# Revit family: TY-B-TY4851_Metric
name_source: partatom
category: Sprinklers
units: mm (PartAtom-declared; Revit-internal decimal feet)

## family parameters
Always vertical = Yes
Cut with Voids When Loaded = No
Maintain Annotation Orientation = No
OmniClass Number = 23.65.70.17.11.24
OmniClass Title = Fire Fighting Sprinkler Heads
Part Type = Normal
Room Calculation Point = No
Round Connector Dimension = Use Diameter
Shared = No
Work Plane-Based = No

## types (42) — shared parameters
COBie = Yes
COBie.Component.Name = Sprinklers:Upright_SIN
COBie.Type = Yes
COBie.Type.AssetType = Fixed
COBie.Type.Category = Pr_70_55_97_84:Sprinklers
COBie.Type.DurationUnit = year
COBie.Type.Manufacturer = Tyco Fire Protection Products
COBie.Type.Material = Bronze
COBie.Type.Shape = Cylinder
COBie.Type.Size = 1/2"(DN15)
Coverage = Standard
Coverage_ = Standard
K-Factor = 114.87
Manufacturer = Tyco Fire Protection Products
Manufacturer URL = www.tyco-fire.com
Material_ = Bronze
Model = TY-B
Nominal Diameter 1 = 15 mm
Orifice = Extra Large
Orifice Size = 13 mm
Outside Diameter 1 = 21 mm
Response = Standard
Response_ = Standard
SIN No = TY4851
Takeout 1 = 56 mm
Technical Data Sheet No = TFP151
zero-valued in all types: COBie.Type.NominalHeight, COBie.Type.NominalLength, COBie.Type.NominalWidth, COBie.Type.ReplacementCost, Default Elevation, Style Id

## per-type parameters (varying)
| type | COBie.Component.Description | COBie.Type.Colour | COBie.Type.Finish | COBie.Type.ModelNumber | COBie.Type.ModelReference | COBie.Type.WarrantyGuarantorParts | Description | Finish_ | Part No | Temperature Rating |
| Upright ½" NPT 57°C  Brass_57-560-1-135 | TY-B Wet Upright  135°F K8.0 1/2 NPT Br | Yellow | Natural Brass | 57-560-1-135 | TY-B Wet Upright  135°F K8.0 1/2 NPT Br | http://tycofsbp.com
TFPPTerms_of_Sale.pdf | TY-B Upright Brass 57°C 8K ½" NPT | Natural Brass | 57-560-1-135 | 57 °C |
| Upright ½" NPT 68°C Brass_57-560-1-155 | TY-B Wet Upright  155°F K8.0 1/2 NPT Br | Yellow | Natural Brass | 57-560-1-155 | TY-B Wet Upright  155°F K8.0 1/2 NPT Br | http://tycofsbp.com
TFPPTerms_of_Sale.pdf | TY-B Upright Brass 68°C 8K ½" NPT | Natural Brass | 57-560-1-155 | 68 °C |
| Upright ½" NPT 79°C Brass_57-560-1-175 | TY-B Wet Upright  175°F K8.0 1/2 NPT Br | Yellow | Natural Brass | 57-560-1-175 | TY-B Wet Upright  175°F K8.0 1/2 NPT Br | http://tycofsbp.com
TFPPTerms_of_Sale.pdf | TY-B Upright Brass 79°C 8K ½" NPT | Natural Brass | 57-560-1-175 | 79 °C |
| Upright ½" NPT 93°C Brass_57-560-1-200 | TY-B Wet Upright  200°F K8.0 1/2 NPT Br | Yellow | Natural Brass | 57-560-1-200 | TY-B Wet Upright  200°F K8.0 1/2 NPT Br | http://tycofsbp.com
TFPPTerms_of_Sale.pdf | TY-B Upright Brass 93°C 8K ½" NPT | Natural Brass | 57-560-1-200 | 93 °C |
| Upright ½" NPT 141°C Brass_57-560-1-286 | TY-B Wet Upright  286°F K8.0 1/2 NPT Br | Yellow | Natural Brass | 57-560-1-286 | TY-B Wet Upright  286°F K8.0 1/2 NPT Br | http://tycofsbp.com
TFPPTerms_of_Sale.pdf | TY-B Upright Brass 141°C 8K ½" NPT | Natural Brass | 57-560-1-286 | 141 °C |
| Upright ½" NPT 182°C Brass_57-560-1-360 | TY-B Wet Upright  360°F K8.0 1/2 NPT Br | Yellow | Natural Brass | 57-560-1-360 | TY-B Wet Upright  360°F K8.0 1/2 NPT Br | http://tycofsbp.com
TFPPTerms_of_Sale.pdf | TY-B Upright Brass 182°C 8K ½" NPT | Natural Brass | 57-560-1-360 | 182 °C |
| Upright ½" NPT 57°C White_57-560-3-135 | TY-B Wet Upright  135°F K8.0 1/2 NPT Wh9010 | White | Pure White | 57-560-3-135 | TY-B Wet Upright  135°F K8.0 1/2 NPT Wh9010 | http://tycofsbp.com
TFPPTerms_of_Sale.pdf | TY-B Upright White 57°C 8K ½" NPT | White RAL9010 | 57-560-3-135 | 57 °C |
| Upright ½" NPT 68°C White_57-560-3-155 | TY-B Wet Upright  155°F K8.0 1/2 NPT Wh9010 | White | Pure White | 57-560-3-155 | TY-B Wet Upright  155°F K8.0 1/2 NPT Wh9010 | http://tycofsbp.com
TFPPTerms_of_Sale.pdf | TY-B Upright White 68°C 8K ½" NPT | White RAL9010 | 57-560-3-155 | 68 °C |
| Upright ½" NPT 79°C White_57-560-3-175 | TY-B Wet Upright  175°F K8.0 1/2 NPT Wh9010 | White | Pure White | 57-560-3-175 | TY-B Wet Upright  175°F K8.0 1/2 NPT Wh9010 | http://tycofsbp.com
TFPPTerms_of_Sale.pdf | TY-B Upright White 79°C 8K ½" NPT | White RAL9010 | 57-560-3-175 | 79 °C |
| Upright ½" NPT 93°C White_57-560-3-200 | TY-B Wet Upright  200°F K8.0 1/2 NPT Wh9010 | White | Pure White | 57-560-3-200 | TY-B Wet Upright  200°F K8.0 1/2 NPT Wh9010 | http://tycofsbp.com
TFPPTerms_of_Sale.pdf | TY-B Upright White 93°C 8K ½" NPT | White RAL9010 | 57-560-3-200 | 93 °C |
| Upright ½" NPT 141°C White_57-560-3-286 | TY-B Wet Upright  286°F K8.0 1/2 NPT Wh9010 | White | Pure White | 57-560-3-286 | TY-B Wet Upright  286°F K8.0 1/2 NPT Wh9010 | http://tycofsbp.com
TFPPTerms_of_Sale.pdf | TY-B Upright White 141°C 8K ½" NPT | White RAL9010 | 57-560-3-286 | 141 °C |
| Upright ½" NPT 182°C White_57-560-3-360 | TY-B Wet Upright  360°F K8.0 1/2 NPT Wh9010 | White | Pure White | 57-560-3-360 | TY-B Wet Upright  360°F K8.0 1/2 NPT Wh9010 | http://tycofsbp.com
TFPPTerms_of_Sale.pdf | TY-B Upright White 182°C 8K ½" NPT | White RAL9010 | 57-560-3-360 | 182 °C |
| Upright ½" NPT 57°C White_57-560-4-135 | TY-B Wet Upright  135°F K8.0 1/2 NPT Wh9003 | White | Signal White | 57-560-4-135 | TY-B Wet Upright  135°F K8.0 1/2 NPT Wh9003 | http://tycofsbp.com | TY-B Upright White 57°C 8K ½" NPT | White RAL9003 | 57-560-4-135 | 57 °C |
| Upright ½" NPT 68°C White_57-560-4-155 | TY-B Wet Upright  155°F K8.0 1/2 NPT Wh9003 | White | Signal White | 57-560-4-155 | TY-B Wet Upright  155°F K8.0 1/2 NPT Wh9003 | http://tycofsbp.com | TY-B Upright White 68°C 8K ½" NPT | White RAL9003 | 57-560-4-155 | 68 °C |
| Upright ½" NPT 79°C White_57-560-4-175 | TY-B Wet Upright  175°F K8.0 1/2 NPT Wh9003 | White | Signal White | 57-560-4-175 | TY-B Wet Upright  175°F K8.0 1/2 NPT Wh9003 | http://tycofsbp.com | TY-B Upright White 79°C 8K ½" NPT | White RAL9003 | 57-560-4-175 | 79 °C |
| Upright ½" NPT 93°C White_57-560-4-200 | TY-B Wet Upright  200°F K8.0 1/2 NPT Wh9003 | White | Signal White | 57-560-4-200 | TY-B Wet Upright  200°F K8.0 1/2 NPT Wh9003 | http://tycofsbp.com | TY-B Upright White 93°C 8K ½" NPT | White RAL9003 | 57-560-4-200 | 93 °C |
| Upright ½" NPT 141°C White_57-560-4-286 | TY-B Wet Upright  286°F K8.0 1/2 NPT Wh9003 | White | Signal White | 57-560-4-286 | TY-B Wet Upright  286°F K8.0 1/2 NPT Wh9003 | http://tycofsbp.com | TY-B Upright White 141°C 8K ½" NPT | White RAL9003 | 57-560-4-286 | 141 °C |
| Upright ½" NPT 182°C White_57-560-4-360 | TY-B Wet Upright  360°F K8.0 1/2 NPT Wh9003 | White | Signal White | 57-560-4-360 | TY-B Wet Upright  360°F K8.0 1/2 NPT Wh9003 | http://tycofsbp.com | TY-B Upright White 182°C 8K ½" NPT | White RAL9003 | 57-560-4-360 | 182 °C |
| Upright ½" NPT 68°C JetBlack_57-560-5-155 | TY-B Wet Upright  155°F K8.0 1/2 NPT JBlk | Black | Jet Black | 57-560-5-155 | TY-B Wet Upright  155°F K8.0 1/2 NPT JBlk | http://tycofsbp.com | TY-B Upright JetBlack 68°C 8K ½" NPT | JetBlack RAL9005 | 57-560-5-155 | 68 °C |
| Upright ½" NPT 68°C  JetBlack_57-560-5-200 | TY-B Wet Upright_Black_155   155°F K8.0 1/2 NPT JBlk | Black | Jet Black | 57-560-5-200 | TY-B Wet Upright_Black_155   155°F K8.0 1/2 NPT JBlk | http://tycofsbp.com | TY-B Upright JetBlack 68°C 8K ½" NPT | Jet Black RAL9005 | 57-560-5-200 | 68 °C |
| Upright ½" NPT 57°C Wax_57-560-6-135 | TY-B Wet Upright  57.2°C K115 DN15 NPT Wx | Gray | Wax Coated | 57-560-6-135 | TY-B Wet Upright  57.2°C K115 DN15 NPT Wx | http://tycofsbp.com | TY-B Upright Wax 57°C 8K ½" NPT | Wax Coated | 57-560-6-135 | 57 °C |
| Upright ½" NPT 68°C Wax_57-560-6-155 | TY-B Wet Upright  68.3°C K115 DN15 NPT Wx | Gray | Wax Coated | 57-560-6-155 | TY-B Wet Upright  68.3°C K115 DN15 NPT Wx | http://tycofsbp.com | TY-B Upright Wax 68°C 8K ½" NPT | Wax Coated | 57-560-6-155 | 68 °C |
| Upright ½" NPT 79°C Wax_57-560-6-175 | TY-B Wet Upright  79.4°C K115 DN15 NPT Wx | Gray | Wax Coated | 57-560-6-175 | TY-B Wet Upright  79.4°C K115 DN15 NPT Wx | http://tycofsbp.com | TY-B Upright Wax 79°C 8K ½" NPT | Wax Coated | 57-560-6-175 | 79 °C |
| Upright ½" NPT 93°C Wax_57-560-6-200 | TY-B Wet Upright  93.3°C K115 DN15 NPT Wx | Gray | Wax Coated | 57-560-6-200 | TY-B Wet Upright  93.3°C K115 DN15 NPT Wx | http://tycofsbp.com | TY-B Upright Wax 93°C 8K ½" NPT | Wax Coated | 57-560-6-200 | 93 °C |
| Upright ½" NPT 141°C Wax_57-560-6-286 | TY-B Wet Upright  141.1°C K115 DN15 NPT Wx | Gray | Wax Coated | 57-560-6-286 | TY-B Wet Upright  141.1°C K115 DN15 NPT Wx | http://tycofsbp.com | TY-B Upright Wax 141°C 8K ½" NPT | Wax Coated | 57-560-6-286 | 141 °C |
| Upright ½" NPT 57°C  Lead_57-560-7-135 | TY-B Wet Upright  57.2°C K115 DN15 NPT Lead | Gray | Lead Coated | 57-560-7-135 | TY-B Wet Upright  57.2°C K115 DN15 NPT Lead | http://tycofsbp.com | TY-B Upright Lead 57°C 8K ½" NPT | Lead Coated | 57-560-7-135 | 57 °C |
| Upright ½" NPT 68°C Lead_57-560-7-155 | TY-B Wet Upright  68.3°C K115 DN15 NPT Lead | Gray | Lead Coated | 57-560-7-155 | TY-B Wet Upright  68.3°C K115 DN15 NPT Lead | http://tycofsbp.com | TY-B Upright Lead 68°C 8K ½" NPT | Lead Coated | 57-560-7-155 | 68 °C |
| Upright ½" NPT 79°C Lead_57-560-7-175 | TY-B Wet Upright  79.4°C K115 DN15 NPT Lead | Gray | Lead Coated | 57-560-7-175 | TY-B Wet Upright  79.4°C K115 DN15 NPT Lead | http://tycofsbp.com | TY-B Upright Lead 79°C 8K ½" NPT | Lead Coated | 57-560-7-175 | 79 °C |
| Upright ½" NPT 93°C Lead_57-560-7-200 | TY-B Wet Upright  93.3°C K115 DN15 NPT Lead | Gray | Lead Coated | 57-560-7-200 | TY-B Wet Upright  93.3°C K115 DN15 NPT Lead | http://tycofsbp.com | TY-B Upright Lead 93°C 8K ½" NPT | Lead Coated | 57-560-7-200 | 93 °C |
| Upright ½" NPT 141°C Lead_57-560-7-286 | TY-B Wet Upright  141.1°C K115 DN15 NPT Lead | Gray | Lead Coated | 57-560-7-286 | TY-B Wet Upright  141.1°C K115 DN15 NPT Lead | http://tycofsbp.com | TY-B Upright Lead 141°C 8K ½" NPT | Lead Coated | 57-560-7-286 | 141 °C |
| Upright ½" NPT 182°C Lead_57-560-7-360 | TY-B Wet Upright  182.2°C K115 DN15 NPT Lead | Gray | Lead Coated | 57-560-7-360 | TY-B Wet Upright  182.2°C K115 DN15 NPT Lead | http://tycofsbp.com | TY-B Upright Lead 182°C 8K ½" NPT | Lead Coated | 57-560-7-360 | 182 °C |
| Upright ½" NPT 57°C Wax Over Lead_57-560-8-135 | TY-B Wet Upright  57.2°C K115 DN15 NPT WoL | Gray | Wax Over Lead | 57-560-8-135 | TY-B Wet Upright  57.2°C K115 DN15 NPT WoL | http://tycofsbp.com | TY-B Upright Wax over Lead 57°C 8K ½" NPT | Wax Over Lead | 57-560-8-135 | 57 °C |
| Upright ½" NPT 68°C Wax Over Lead_57-560-8-155 | TY-B Wet Upright  68.3°C K115 DN15 NPT WoL | Gray | Wax Over Lead | 57-560-8-155 | TY-B Wet Upright  68.3°C K115 DN15 NPT WoL | http://tycofsbp.com | TY-B Upright Wax over Lead 68°C 8K ½" NPT | Wax Over Lead | 57-560-8-155 | 68 °C |
| Upright ½" NPT 79°C Wax Over Lead_57-560-8-175 | TY-B Wet Upright  79.4°C K115 DN15 NPT WoL | Gray | Wax Over Lead | 57-560-8-175 | TY-B Wet Upright  79.4°C K115 DN15 NPT WoL | http://tycofsbp.com | TY-B Upright Wax over Lead 79°C 8K ½" NPT | Wax Over Lead | 57-560-8-175 | 79 °C |
| Upright ½" NPT 93°C Wax Over Lead_57-560-8-200 | TY-B Wet Upright  93.3°C K115 DN15 NPT WoL | Gray | Wax Over Lead | 57-560-8-200 | TY-B Wet Upright  93.3°C K115 DN15 NPT WoL | http://tycofsbp.com | TY-B Upright Wax over Lead 93°C 8K ½" NPT | Wax Over Lead | 57-560-8-200 | 93 °C |
| Upright ½" NPT 141°C Wax Over Lead_57-560-8-286 | TY-B Wet Upright  141.1°C K115 DN15 NPT WoL | Gray | Wax over Lead | 57-560-8-286 | TY-B Wet Upright  141.1°C K115 DN15 NPT WoL | http://tycofsbp.com | TY-B Upright Wax over Lead 141°C 8K ½" NPT | Wax Over Lead | 57-560-8-286 | 141 °C |
| Upright ½" NPT 57°C Chrome_57-560-9-135 | TY-B Wet Upright  135°F K8.0 1/2 NPT Chr | White | Pure White | 57-560-9-135 | TY-B Wet Upright  135°F K8.0 1/2 NPT Chr | http://tycofsbp.com
TFPPTerms_of_Sale.pdf | TY-B Upright Chrome 57°C 8K ½" NPT | Chrome Plated | 57-560-9-135 | 57 °C |
| Upright ½" NPT 68°C Chrome_57-560-9-155 | TY-B Wet Upright  155°F K8.0 1/2 NPT Chr | Silver | Chrome Plated | 57-560-9-155 | TY-B Wet Upright  155°F K8.0 1/2 NPT Chr | http://tycofsbp.com
TFPPTerms_of_Sale.pdf | TY-B Upright Chrome 68°C 8K ½" NPT | Chrome Plated | 57-560-9-155 | 68 °C |
| Upright ½" NPT 79°C Chrome_57-560-9-175 | TY-B Wet Upright  175°F K8.0 1/2 NPT Chr | Silver | Chrome Plated | 57-560-9-175 | TY-B Wet Upright  175°F K8.0 1/2 NPT Chr | http://tycofsbp.com
TFPPTerms_of_Sale.pdf | TY-B Upright Chrome 79°C 8K ½" NPT | Chrome Plated | 57-560-9-175 | 79 °C |
| Upright ½" NPT 93°C Chrome_57-560-9-200 | TY-B Wet Upright  200°F K8.0 1/2 NPT Chr | Silver | Chrome Plated | 57-560-9-200 | TY-B Wet Upright  200°F K8.0 1/2 NPT Chr | http://tycofsbp.com
TFPPTerms_of_Sale.pdf | TY-B Upright Chrome 93°C 8K ½" NPT | Chrome Plated | 57-560-9-200 | 93 °C |
| Upright ½" NPT 141°C Chrome_57-560-9-286 | TY-B Wet Upright  286°F K8.0 1/2 NPT Chr | Silver | Chrome Plated | 57-560-9-286 | TY-B Wet Upright  286°F K8.0 1/2 NPT Chr | http://tycofsbp.com
TFPPTerms_of_Sale.pdf | TY-B Upright Chrome 141°C 8K ½" NPT | Chrome Plated | 57-560-9-286 | 141 °C |
| Upright ½" NPT 182°C Chrome_57-560-9-360 | TY-B Wet Upright  360°F K8.0 1/2 NPT Chr | Silver | Chrome Plated | 57-560-9-360 | TY-B Wet Upright  360°F K8.0 1/2 NPT Chr | http://tycofsbp.com
TFPPTerms_of_Sale.pdf | TY-B Upright Chrome 182°C 8K ½" NPT | Chrome plated | 57-560-9-360 | 182 °C |

## geometry (parser evidence)
native form markers: Blend x2, Sweep x62
no freeform markers — native parametric forms only
